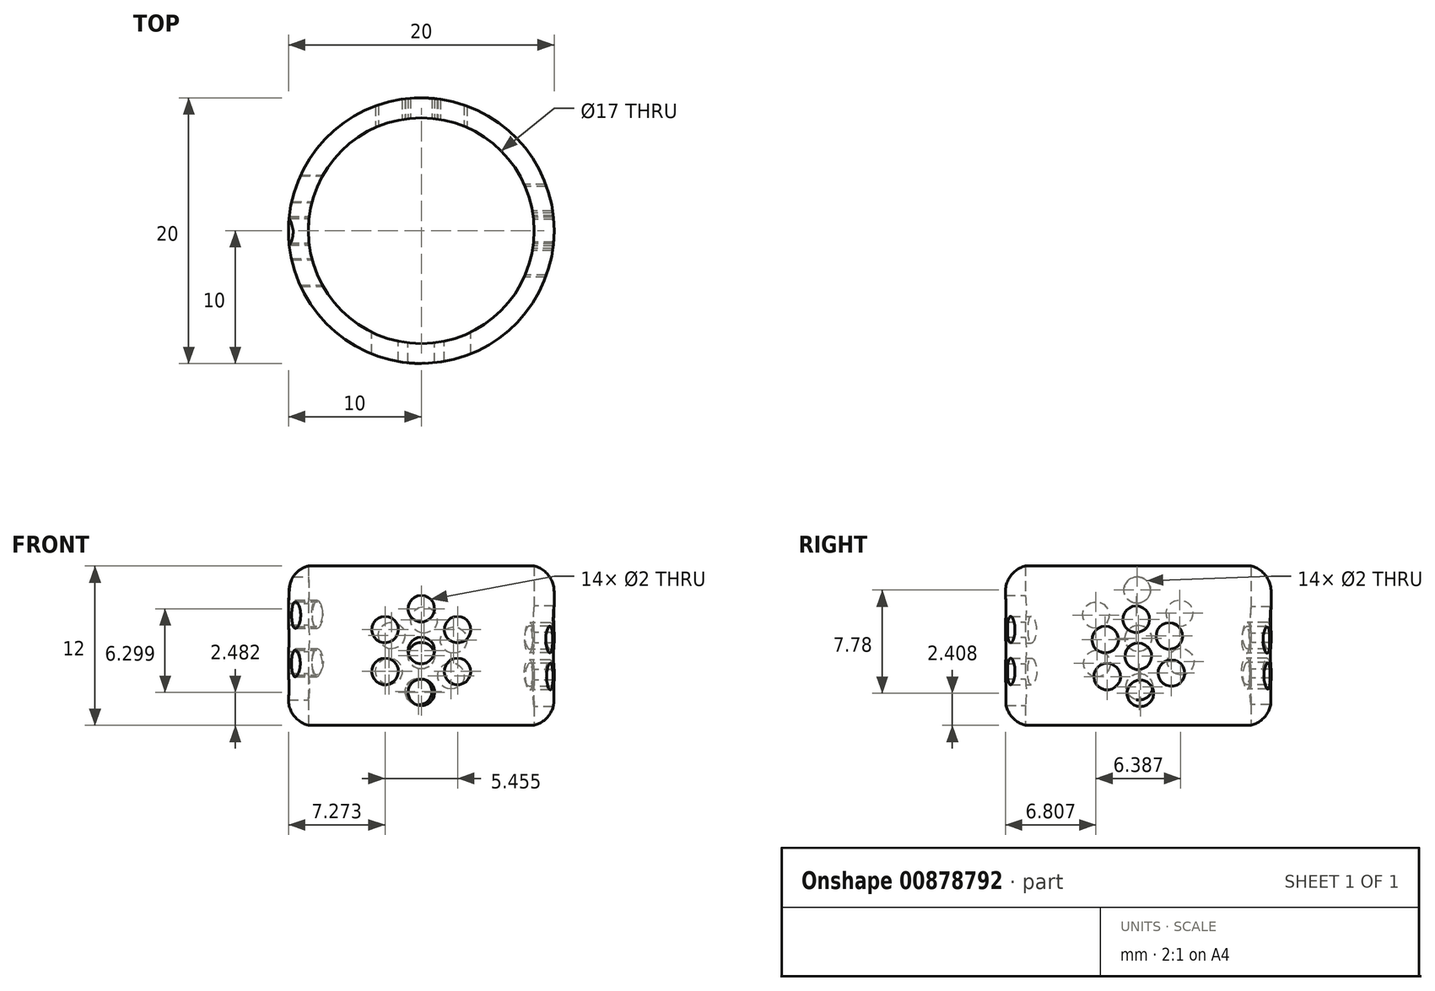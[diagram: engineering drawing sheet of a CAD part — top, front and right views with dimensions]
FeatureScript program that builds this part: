
annotation { "Feature Type Name" : "Feature", "Feature Type Description" : "" }
export const myFeature = defineFeature(function(context is Context, id is Id, definition is map)
    precondition{}
    {
        {
            var Q0;
            Q0=qCreatedBy(makeId("Top.planeOp"),FACE);
            var sketch = newSketch(context, id + "F0", { "sketchPlane" : qUnion([Q0])});
            skCircle(sketch, "E0", {"center": v(0, 0) * mm, "radius": 10 * mm});
            skCircle(sketch, "E1", {"center": v(0, 0) * mm, "radius": 8.5 * mm});
            skSolve(sketch);
        }
        {
            var Q0;
            Q0=makeQuery(id+"F0.imprint","IMPRINT",FACE,{"disambiguationData":[TD([[makeQuery(id+"F0.imprint","IMPRINT",EDGE,{"derivedFrom":sQuery(id+"F0.wireOp",EDGE,"E0")}),1.0]])]});
            extrude(context, id + "F1", {"entities" : qUnion([Q0]), "depth" : 12 * mm, "offsetDistance" : 25.4 * mm});
        }
        {
            var Q0;
            Q0=makeQuery(id+"F1.opExtrude","CAP_EDGE",EDGE,{"disambiguationData":[OSD([sQuery(id+"F0.wireOp",EDGE,"E0")])],"isStart":false});
            var Q1;
            Q1=makeQuery(id+"F1.opExtrude","CAP_EDGE",EDGE,{"disambiguationData":[OSD([sQuery(id+"F0.wireOp",EDGE,"E0")])],"isStart":true});
            fillet(context, id + "F2", {"entities" : qUnion([Q0, Q1]), "radius" : 2 * mm, "tangentPropagation" : true, "allowEdgeOverflow" : false});
        }
        {
            var Q0;
            Q0=qCreatedBy(makeId("Front.planeOp"),FACE);
            var sketch = newSketch(context, id + "F3", { "sketchPlane" : qUnion([Q0])});
            skCircle(sketch, "E2.cCircle", {"center": v(0, 5.63) * mm, "radius": 2.73 * mm, "construction": true});
            skLineSegment(sketch, "E2.0", {"start": v(-2.73, 4.06) * mm, "end": v(-2.73, 7.2) * mm});
            skLineSegment(sketch, "E2.1", {"start": v(-2.73, 7.2) * mm, "end": v(0, 8.78) * mm});
            skLineSegment(sketch, "E2.2", {"start": v(0, 8.78) * mm, "end": v(2.73, 7.2) * mm});
            skLineSegment(sketch, "E2.3", {"start": v(2.73, 7.2) * mm, "end": v(2.73, 4.06) * mm});
            skLineSegment(sketch, "E2.4", {"start": v(2.73, 4.06) * mm, "end": v(0, 2.48) * mm});
            skLineSegment(sketch, "E2.5", {"start": v(0, 2.48) * mm, "end": v(-2.73, 4.06) * mm});
            skPoint(sketch, "E2.0.midPoint", {"position": v(-2.73, 5.63) * mm});
            skSolve(sketch);
        }
        {
            var Q0;
            Q0=sQuery(id+"F3.wireOp",VERTEX,"E2.1.end");
            var Q1;
            Q1=sQuery(id+"F3.wireOp",VERTEX,"E2.2.end");
            var Q2;
            Q2=sQuery(id+"F3.wireOp",VERTEX,"E2.3.end");
            var Q3;
            Q3=sQuery(id+"F3.wireOp",VERTEX,"E2.4.end");
            var Q4;
            Q4=sQuery(id+"F3.wireOp",VERTEX,"E2.0.start");
            var Q5;
            Q5=sQuery(id+"F3.wireOp",VERTEX,"E2.0.end");
            var Q6;
            Q6=sQuery(id+"F3.wireOp",VERTEX,"E2.cCircle.center");
            var Q7;
            Q7=makeQuery(id+"F1.opExtrude","SWEPT_BODY",BODY,{"disambiguationData":[OSD([sQuery(id+"F0.wireOp",EDGE,"E0"),sQuery(id+"F0.wireOp",EDGE,"E1")])]});
            hole(context, id + "F4", {"style" : HoleStyle.SIMPLE, "endStyle" : HoleEndStyle.THROUGH, "oppositeDirection" : true, "holeDiameter" : 2 * mm, "majorDiameter" : 6.35 * mm, "isTappedThrough" : true, "tappedDepth" : 12.7 * mm, "tapClearance" : 3, "locations" : qUnion([Q0, Q1, Q2, Q3, Q4, Q5, Q6]), "scope" : qUnion([Q7])});
        }
        {
            var Q0;
            Q0=qCreatedBy(makeId("Right.planeOp"),FACE);
            var sketch = newSketch(context, id + "F5", { "sketchPlane" : qUnion([Q0])});
            skCircle(sketch, "E3.cCircle", {"center": v(0, 5.2) * mm, "radius": 2.42 * mm, "construction": true});
            skLineSegment(sketch, "E3.0", {"start": v(-0.15, 7.99) * mm, "end": v(2.34, 6.72) * mm});
            skLineSegment(sketch, "E3.1", {"start": v(2.34, 6.72) * mm, "end": v(2.5, 3.94) * mm});
            skLineSegment(sketch, "E3.2", {"start": v(2.5, 3.94) * mm, "end": v(0.15, 2.4) * mm});
            skLineSegment(sketch, "E3.3", {"start": v(0.15, 2.4) * mm, "end": v(-2.34, 3.67) * mm});
            skLineSegment(sketch, "E3.4", {"start": v(-2.34, 3.67) * mm, "end": v(-2.5, 6.46) * mm});
            skLineSegment(sketch, "E3.5", {"start": v(-2.5, 6.46) * mm, "end": v(-0.15, 7.99) * mm});
            skPoint(sketch, "E3.0.midPoint", {"position": v(1.1, 7.36) * mm});
            skSolve(sketch);
        }
        {
            var Q0;
            Q0=sQuery(id+"F5.wireOp",VERTEX,"E3.0.start");
            var Q1;
            Q1=sQuery(id+"F5.wireOp",VERTEX,"E3.0.end");
            var Q2;
            Q2=sQuery(id+"F5.wireOp",VERTEX,"E3.1.end");
            var Q3;
            Q3=sQuery(id+"F5.wireOp",VERTEX,"E3.2.end");
            var Q4;
            Q4=sQuery(id+"F5.wireOp",VERTEX,"E3.3.end");
            var Q5;
            Q5=sQuery(id+"F5.wireOp",VERTEX,"E3.4.end");
            var Q6;
            Q6=sQuery(id+"F5.wireOp",VERTEX,"E3.cCircle.center");
            var Q7;
            Q7=makeQuery(id+"F1.opExtrude","SWEPT_BODY",BODY,{"disambiguationData":[OSD([sQuery(id+"F0.wireOp",EDGE,"E0"),sQuery(id+"F0.wireOp",EDGE,"E1")])]});
            hole(context, id + "F6", {"style" : HoleStyle.SIMPLE, "endStyle" : HoleEndStyle.THROUGH, "oppositeDirection" : true, "holeDiameter" : 2 * mm, "majorDiameter" : 6.35 * mm, "isTappedThrough" : true, "tappedDepth" : 12.7 * mm, "tapClearance" : 3, "locations" : qUnion([Q0, Q1, Q2, Q3, Q4, Q5, Q6]), "scope" : qUnion([Q7])});
        }
        {
            var Q0;
            Q0=qCreatedBy(makeId("Front.planeOp"),FACE);
            var sketch = newSketch(context, id + "F7", { "sketchPlane" : qUnion([Q0])});
            skCircle(sketch, "E4.cCircle", {"center": v(0, 5.24) * mm, "radius": 2.34 * mm, "construction": true});
            skLineSegment(sketch, "E4.0", {"start": v(0.2, 7.94) * mm, "end": v(2.43, 6.42) * mm});
            skLineSegment(sketch, "E4.1", {"start": v(2.43, 6.42) * mm, "end": v(2.24, 3.72) * mm});
            skLineSegment(sketch, "E4.2", {"start": v(2.24, 3.72) * mm, "end": v(-0.2, 2.55) * mm});
            skLineSegment(sketch, "E4.3", {"start": v(-0.2, 2.55) * mm, "end": v(-2.43, 4.07) * mm});
            skLineSegment(sketch, "E4.4", {"start": v(-2.43, 4.07) * mm, "end": v(-2.24, 6.76) * mm});
            skLineSegment(sketch, "E4.5", {"start": v(-2.24, 6.76) * mm, "end": v(0.2, 7.94) * mm});
            skPoint(sketch, "E4.0.midPoint", {"position": v(1.32, 7.18) * mm});
            skSolve(sketch);
        }
        {
            var Q0;
            Q0=sQuery(id+"F7.wireOp",VERTEX,"E4.0.start");
            var Q1;
            Q1=sQuery(id+"F7.wireOp",VERTEX,"E4.cCircle.center");
            var Q2;
            Q2=sQuery(id+"F7.wireOp",VERTEX,"E4.0.end");
            var Q3;
            Q3=sQuery(id+"F7.wireOp",VERTEX,"E4.1.end");
            var Q4;
            Q4=sQuery(id+"F7.wireOp",VERTEX,"E4.2.end");
            var Q5;
            Q5=sQuery(id+"F7.wireOp",VERTEX,"E4.3.end");
            var Q6;
            Q6=sQuery(id+"F7.wireOp",VERTEX,"E4.4.end");
            var Q7;
            Q7=makeQuery(id+"F1.opExtrude","SWEPT_BODY",BODY,{"disambiguationData":[OSD([sQuery(id+"F0.wireOp",EDGE,"E0"),sQuery(id+"F0.wireOp",EDGE,"E1")])]});
            hole(context, id + "F8", {"style" : HoleStyle.SIMPLE, "endStyle" : HoleEndStyle.THROUGH, "holeDiameter" : 2 * mm, "majorDiameter" : 6.35 * mm, "isTappedThrough" : true, "tappedDepth" : 12.7 * mm, "tapClearance" : 3, "locations" : qUnion([Q0, Q1, Q2, Q3, Q4, Q5, Q6]), "scope" : qUnion([Q7])});
        }
        {
            var Q0;
            Q0=qCreatedBy(makeId("Right.planeOp"),FACE);
            var sketch = newSketch(context, id + "F9", { "sketchPlane" : qUnion([Q0])});
            skCircle(sketch, "E5.cCircle", {"center": v(0, 6.55) * mm, "radius": 3.15 * mm, "construction": true});
            skLineSegment(sketch, "E5.0", {"start": v(3.2, 4.8) * mm, "end": v(0.08, 2.9) * mm});
            skLineSegment(sketch, "E5.1", {"start": v(0.08, 2.9) * mm, "end": v(-3.11, 4.66) * mm});
            skLineSegment(sketch, "E5.2", {"start": v(-3.11, 4.66) * mm, "end": v(-3.2, 8.3) * mm});
            skLineSegment(sketch, "E5.3", {"start": v(-3.2, 8.3) * mm, "end": v(-0.08, 10.19) * mm});
            skLineSegment(sketch, "E5.4", {"start": v(-0.08, 10.19) * mm, "end": v(3.11, 8.44) * mm});
            skLineSegment(sketch, "E5.5", {"start": v(3.11, 8.44) * mm, "end": v(3.2, 4.8) * mm});
            skPoint(sketch, "E5.0.midPoint", {"position": v(1.64, 3.85) * mm});
            skSolve(sketch);
        }
        {
            var Q0;
            Q0=sQuery(id+"F9.wireOp",VERTEX,"E5.3.end");
            var Q1;
            Q1=sQuery(id+"F9.wireOp",VERTEX,"E5.cCircle.center");
            var Q2;
            Q2=sQuery(id+"F9.wireOp",VERTEX,"E5.4.end");
            var Q3;
            Q3=sQuery(id+"F9.wireOp",VERTEX,"E5.0.start");
            var Q4;
            Q4=sQuery(id+"F9.wireOp",VERTEX,"E5.1.end");
            var Q5;
            Q5=sQuery(id+"F9.wireOp",VERTEX,"E5.2.end");
            var Q6;
            Q6=sQuery(id+"F9.wireOp",VERTEX,"E5.0.end");
            var Q7;
            Q7=makeQuery(id+"F1.opExtrude","SWEPT_BODY",BODY,{"disambiguationData":[OSD([sQuery(id+"F0.wireOp",EDGE,"E0"),sQuery(id+"F0.wireOp",EDGE,"E1")])]});
            hole(context, id + "F10", {"style" : HoleStyle.SIMPLE, "endStyle" : HoleEndStyle.THROUGH, "holeDiameter" : 2 * mm, "majorDiameter" : 6.35 * mm, "isTappedThrough" : true, "tappedDepth" : 12.7 * mm, "tapClearance" : 3, "locations" : qUnion([Q0, Q1, Q2, Q3, Q4, Q5, Q6]), "scope" : qUnion([Q7])});
        }
    });
